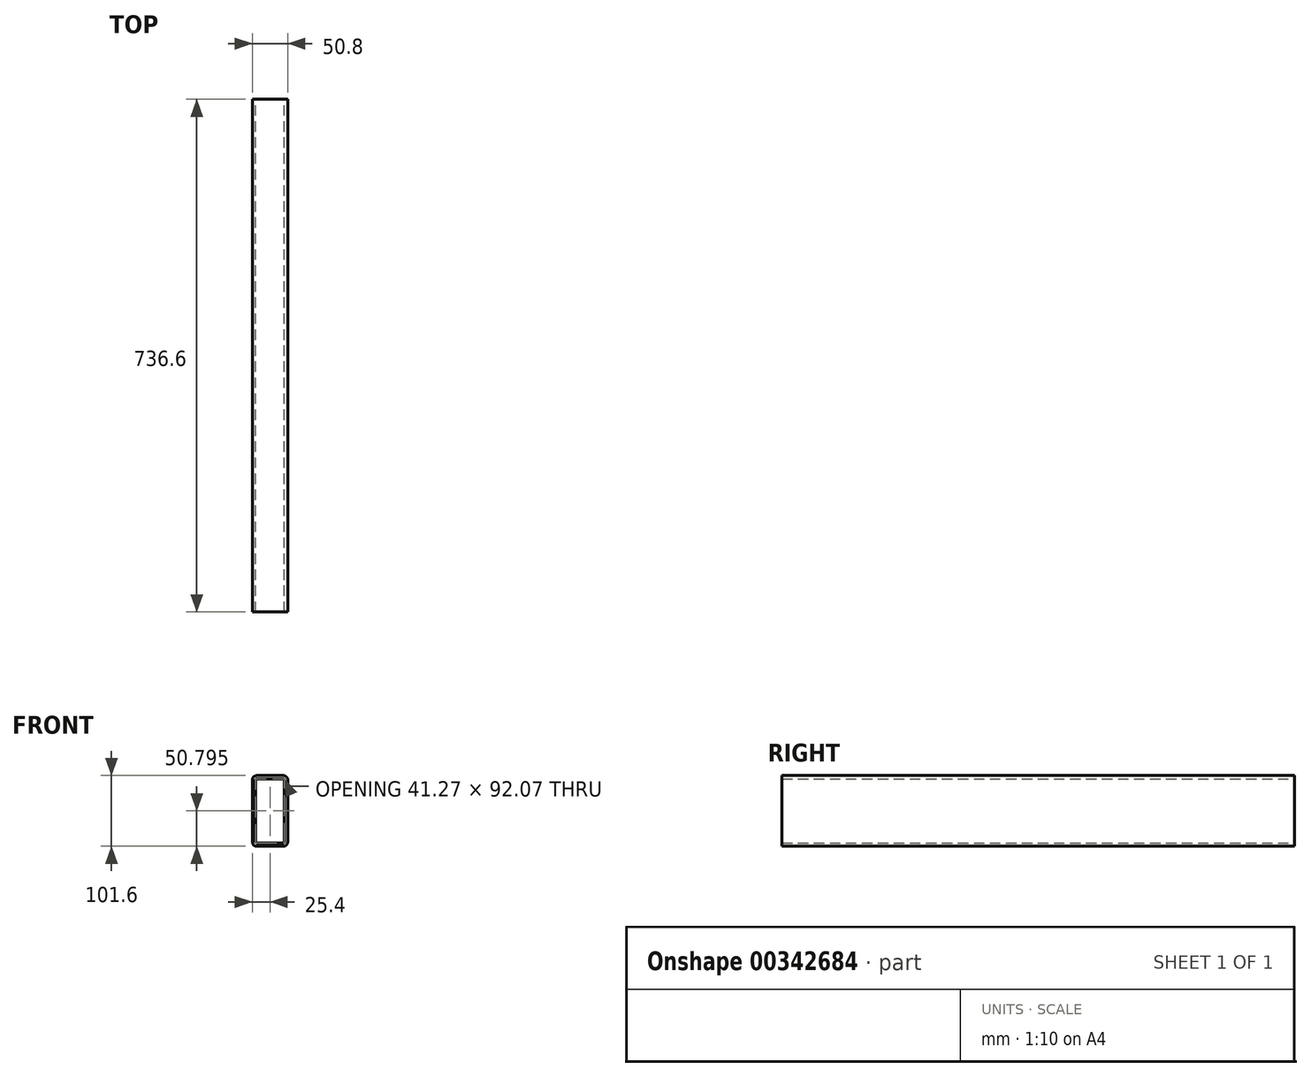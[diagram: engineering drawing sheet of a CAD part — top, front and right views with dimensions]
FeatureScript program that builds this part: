
annotation { "Feature Type Name" : "Feature", "Feature Type Description" : "" }
export const myFeature = defineFeature(function(context is Context, id is Id, definition is map)
    precondition{}
    {
        {
            var Q0;
            Q0=qCreatedBy(makeId("Front.planeOp"),FACE);
            var sketch = newSketch(context, id + "F0", { "sketchPlane" : qUnion([Q0])});
            skLineSegment(sketch, "E0.bottom", {"start": v(-19.05, 50.8) * mm, "end": v(19.05, 50.8) * mm});
            skLineSegment(sketch, "E0.top", {"start": v(-19.05, -50.8) * mm, "end": v(19.05, -50.8) * mm});
            skLineSegment(sketch, "E0.left", {"start": v(-25.4, 44.45) * mm, "end": v(-25.4, -44.45) * mm});
            skLineSegment(sketch, "E0.right", {"start": v(25.4, 44.45) * mm, "end": v(25.4, -44.45) * mm});
            skPoint(sketch, "E0.middle", {"position": v(0, 0) * mm});
            skPoint(sketch, "E1.visualSharp", {"position": v(-25.4, 50.8) * mm});
            skArc(sketch, "E1.filletArc", {"start": v(-19.05, 50.8) * mm, "mid": v(-23.54, 48.94) * mm, "end": v(-25.4, 44.45) * mm});
            skPoint(sketch, "E2.visualSharp", {"position": v(25.4, 50.8) * mm});
            skArc(sketch, "E2.filletArc", {"start": v(25.4, 44.45) * mm, "mid": v(23.54, 48.94) * mm, "end": v(19.05, 50.8) * mm});
            skPoint(sketch, "E3.visualSharp", {"position": v(25.4, -50.8) * mm});
            skArc(sketch, "E3.filletArc", {"start": v(19.05, -50.8) * mm, "mid": v(23.54, -48.94) * mm, "end": v(25.4, -44.45) * mm});
            skPoint(sketch, "E4.visualSharp", {"position": v(-25.4, -50.8) * mm});
            skArc(sketch, "E4.filletArc", {"start": v(-25.4, -44.45) * mm, "mid": v(-23.54, -48.94) * mm, "end": v(-19.05, -50.8) * mm});
            skLineSegment(sketch, "E5.0", {"start": v(-19.05, 46.03) * mm, "end": v(19.05, 46.03) * mm});
            skLineSegment(sketch, "E5.1", {"start": v(-20.64, 44.44) * mm, "end": v(-20.64, -44.45) * mm});
            skLineSegment(sketch, "E5.2", {"start": v(-19.05, -46.04) * mm, "end": v(19.05, -46.04) * mm});
            skLineSegment(sketch, "E5.3", {"start": v(20.64, 44.44) * mm, "end": v(20.64, -44.45) * mm});
            skPoint(sketch, "E6.visualSharp", {"position": v(-20.64, 46.03) * mm});
            skArc(sketch, "E6.filletArc", {"start": v(-19.05, 46.03) * mm, "mid": v(-20.17, 45.56) * mm, "end": v(-20.64, 44.44) * mm});
            skPoint(sketch, "E7.visualSharp", {"position": v(20.64, 46.03) * mm});
            skArc(sketch, "E7.filletArc", {"start": v(20.64, 44.44) * mm, "mid": v(20.17, 45.56) * mm, "end": v(19.05, 46.03) * mm});
            skPoint(sketch, "E8.visualSharp", {"position": v(20.64, -46.04) * mm});
            skArc(sketch, "E8.filletArc", {"start": v(19.05, -46.04) * mm, "mid": v(20.17, -45.57) * mm, "end": v(20.64, -44.45) * mm});
            skPoint(sketch, "E9.visualSharp", {"position": v(-20.64, -46.04) * mm});
            skArc(sketch, "E9.filletArc", {"start": v(-20.64, -44.45) * mm, "mid": v(-20.17, -45.57) * mm, "end": v(-19.05, -46.04) * mm});
            skSolve(sketch);
        }
        {
            var Q0;
            Q0=makeQuery(id+"F0.imprint","IMPRINT",FACE,{"disambiguationData":[TD([[makeQuery(id+"F0.imprint","IMPRINT",EDGE,{"derivedFrom":sQuery(id+"F0.wireOp",EDGE,"E0.bottom")}),-1.0]])]});
            extrude(context, id + "F1", {"entities" : qUnion([Q0]), "depth" : 736.6 * mm});
        }
    });
